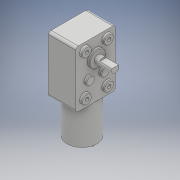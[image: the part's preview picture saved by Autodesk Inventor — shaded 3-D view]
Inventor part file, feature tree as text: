
AUTODESK INVENTOR PART (.ipt)
format: ipt  version: 2017 SP1 (Build 210196100, 196)  size: 350,208 bytes
history: native  units: mm
features: extrude x10, sketch x10, fillet x7, projected_geometry x6, other x1
ambient origin geometry x8: Origin, YZ Plane, XZ Plane, XY Plane, X Axis, Y Axis, Z Axis, Center Point
bodies: Body1 (feature_tree)
feature tree (34):
  other  "Твердое тело1"
  extrude  "Выдавливание1"  Depth=32.0mm
  fillet  "Сопряжение1"  Radius=46.0mm
  extrude  "Выдавливание2"  Depth=22.0mm TaperAngle=0.0deg
  extrude  "Выдавливание3"  Depth=2.0mm
  fillet  "Сопряжение2"  Radius=10.0mm
  extrude  "Выдавливание4"  Depth=14.0mm
  fillet  "Сопряжение3"  Radius=13.0mm
  extrude  "Выдавливание5"  Depth=0.2mm TaperAngle=0.0deg
  fillet  "Сопряжение4"  Radius=24.0mm
  extrude  "Выдавливание6"  Depth=31.0mm TaperAngle=0.0deg
  fillet  "Сопряжение5"  Radius=1.0mm
  extrude  "Выдавливание7"  Depth=0.5mm
  extrude  "Выдавливание8"  Depth=6.0mm
  extrude  "Выдавливание9"  Depth=1.0mm TaperAngle=0.0deg
  extrude  "Выдавливание10"  Depth=0.3mm
  fillet  "Сопряжение6"  Radius=0.2mm
  fillet  "Сопряжение7"  Radius=2.0mm
  sketch  "Эскиз1"
  sketch  "Эскиз2"
  sketch  "Эскиз3"
  sketch  "Эскиз4"
  sketch  "Эскиз5"
  projected_geometry  "Спроецированная петля1"
  projected_geometry  "Спроецированная петля2"
  sketch  "Эскиз6"
  sketch  "Эскиз7"
  projected_geometry  "Спроецированная петля3"
  projected_geometry  "Спроецированная петля4"
  sketch  "Эскиз8"
  projected_geometry  "Спроецированная петля5"
  sketch  "Эскиз9"
  projected_geometry  "Спроецированная петля6"
  sketch  "Эскиз10"
